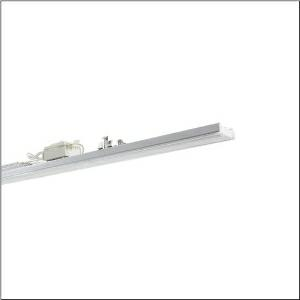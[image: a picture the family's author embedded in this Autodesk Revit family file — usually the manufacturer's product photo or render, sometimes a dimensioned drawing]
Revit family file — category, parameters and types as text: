
# Revit family: licross_21_recessed_ho_52tl12dn4fxm
name_source: partatom
category: Lighting Fixtures
units: mm (PartAtom-declared; Revit-internal decimal feet)

## family parameters
Cut with Voids When Loaded = No
Host = Face
Light Source = No
Part Type = Normal
Room Calculation Point = No
Round Connector Dimension = Use Diameter
Shared = No

## types (1)
- --- (1 x LED, 15000 lm, 84.6 W, 4000K)
    Apparent Load = 85 VA
    CIE Flux Codes = 69 91 98 100 100
    Color Rendering = 80
    Color Temperature = 4000K
    Default Elevation = 1800 mm
    Description = Licross 21 Recessed HO, luminaire insert, of sheet steel, galvanised, coil coated, white, length: 1.500mm, width: 66mm, height: 67mm, LED rated luminous flux: 15.000lm, light colour: 840, SDCM (Standard Deviation of Colour Matching)MacAdam ≤ 3 SDCM (initial), control gear: DALI 2, with plug, 5-pole, with phase selection, mains connection: 220..240V, AC, 50/60Hz, rated input power: 85W, internal wiring halogen-free, primary optical cover: cover, of PMMA, light emission: direct distribution, primary light characteristic: symmetric, protection rating (complete): IP40, insulation class (complete): insulation class I (protective earthing), certification: CE, ENEC, VDE, UKCA, protection symbol: D if used in an environment without relevant dust loads with corresponding accessories, impact resistance: IK06, permissible ambient temperature for indoor applications: -25..+30°C, corresponds to IFS (International Featured Standards) requirements for safety and quality in the food industry, reducing of maximum allowable ambient temperature of 5°C with ceiling mounting, LABS conformity tested according to VDMA 24364:2018-05, The light source and the operating device comply with the requirements of the Ecodesign Regulation (EU) 2019/2020 and are replaceable in accordance with this regulation, packaging unit: 1 piece
    Height = 58 mm
    Lamp = 1 x LED
    Lamp Light Flux = 15000 lm
    Lamp Power = 84.6 W
    Lamp count = 1
    Length = 1500 mm
    Luminous efficacy = 177 lm/W
    Manufacturer = Siteco
    ModVariant = No
    Model = 52TL12DN4FXM
    Mounting Place = Ceiling
    Mounting Type = Pendant
    Number of Poles = 1
    OnlyDefault = Yes
    Power Factor = 1
    Product Name = Licross 21 Recessed HO
    Product group = luminaire insert | ceiling pendant
    ProductGroupID = 901
    Protection Class = Protection class I
    Protection Degree = IP 40
    RLX_Detail_Level = 1
    RLX_Emergency_Light_Flux = 0 lm
    RLX_Emergency_Type = 0
    RLX_Emergency_Type_DB = No
    RlxData = <blob elided: 25005 chars, md5=860c17dd>
    Socket = socket
    Standby Power = 0 W
    System Light Flux = 15000 lm
    System Power = 85 W
    Type Comments = factory setting: luminous flux: 100 % | dim-lin: 254 | 484 mA
    Type Image = l_1296930.jpg
    URL = http://relux.com
    VarID = @adj_116725
    Voltage = 0 V
    Weight = 0.00 kg
    Width = 66 mm

## geometry (parser evidence)
native form markers: Blend x4, Sweep x14
no freeform markers — native parametric forms only
